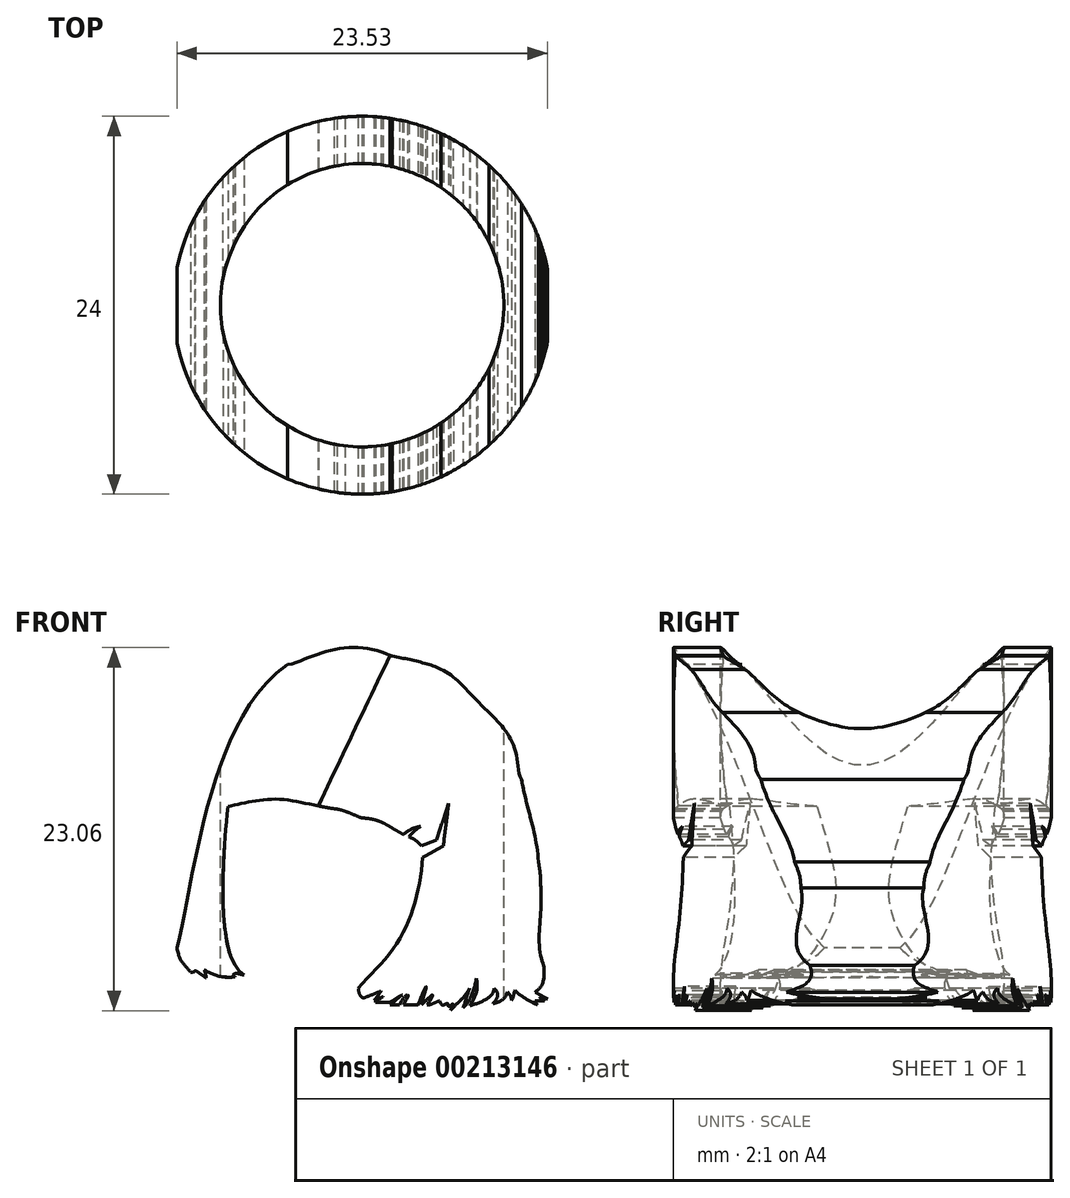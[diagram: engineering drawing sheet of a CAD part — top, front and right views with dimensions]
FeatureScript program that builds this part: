
annotation { "Feature Type Name" : "Feature", "Feature Type Description" : "" }
export const myFeature = defineFeature(function(context is Context, id is Id, definition is map)
    precondition{}
    {
        {
            var Q0;
            Q0=qCreatedBy(makeId("Top.planeOp"),FACE);
            var sketch = newSketch(context, id + "F0", { "sketchPlane" : qUnion([Q0])});
            skCircle(sketch, "E0", {"center": v(0, 0) * mm, "radius": 9 * mm});
            skCircle(sketch, "E1.0", {"center": v(0, 0) * mm, "radius": 12 * mm});
            skSolve(sketch);
        }
        {
            var Q0;
            Q0 = qSketchRegion(id + "F0", true);
            extrude(context, id + "F1", {"entities" : qUnion([Q0]), "oppositeDirection" : true, "depth" : 27.6 * mm});
        }
        {
            var Q0;
            Q0=qCreatedBy(makeId("Front.planeOp"),FACE);
            var sketch = newSketch(context, id + "F2", { "sketchPlane" : qUnion([Q0])});
            skFitSpline(sketch, "E2", {"points": [v(1.9, -2.14) * mm, v(5, -2.98) * mm], "startDerivative": vector(3.67, -0.67) * mm, "endDerivative": vector(1.76, -1) * mm});
            skFitSpline(sketch, "E3", {"points": [v(8.06, -5.72) * mm, v(5, -2.98) * mm], "startDerivative": vector(-3.05, 2.74) * mm, "endDerivative": vector(-3.1, 1.24) * mm});
            skFitSpline(sketch, "E4", {"points": [v(10.12, -9.96) * mm, v(8.06, -5.72) * mm], "startDerivative": vector(-1.55, 2.48) * mm, "endDerivative": vector(-7.13, 6.67) * mm});
            skFitSpline(sketch, "E5", {"points": [v(11.2, -16.16) * mm, v(10.12, -9.96) * mm], "startDerivative": vector(0.31, 6.82) * mm, "endDerivative": vector(-1.19, 6.77) * mm});
            skFitSpline(sketch, "E6", {"points": [v(11.53, -21.8) * mm, v(11.2, -16.16) * mm], "startDerivative": vector(-2.17, 4.8) * mm, "endDerivative": vector(-1.55, 4.96) * mm});
            skFitSpline(sketch, "E7", {"points": [v(11, -23.48) * mm, v(11.53, -21.8) * mm], "startDerivative": vector(1.31, 1.1) * mm, "endDerivative": vector(-0.27, 3.39) * mm});
            skLineSegment(sketch, "E8", {"start": v(11, -23.48) * mm, "end": v(11.77, -23.9) * mm});
            skLineSegment(sketch, "E9", {"start": v(11.77, -23.9) * mm, "end": v(11.27, -23.81) * mm});
            skLineSegment(sketch, "E10", {"start": v(11.27, -23.81) * mm, "end": v(11.58, -24.05) * mm});
            skLineSegment(sketch, "E11", {"start": v(11.58, -24.05) * mm, "end": v(10.97, -24.05) * mm});
            skLineSegment(sketch, "E12", {"start": v(10.97, -24.05) * mm, "end": v(11.13, -24.29) * mm});
            skFitSpline(sketch, "E13", {"points": [v(9.7, -23.36) * mm, v(11.13, -24.29) * mm], "startDerivative": vector(0.83, -1.03) * mm, "endDerivative": vector(1.37, -0.62) * mm});
            skFitSpline(sketch, "E14", {"points": [v(9.49, -24.02) * mm, v(9.7, -23.36) * mm], "startDerivative": vector(0.42, 0.54) * mm, "endDerivative": vector(0.2, 0.6) * mm});
            skFitSpline(sketch, "E15", {"points": [v(9.23, -23.48) * mm, v(9.49, -24.02) * mm], "startDerivative": vector(0.59, -0.48) * mm, "endDerivative": vector(0, -0.4) * mm});
            skFitSpline(sketch, "E16", {"points": [v(8.32, -24.21) * mm, v(9.23, -23.48) * mm], "startDerivative": vector(1.41, 0.44) * mm, "endDerivative": vector(0.57, 1.57) * mm});
            skFitSpline(sketch, "E17", {"points": [v(8.37, -23.25) * mm, v(8.32, -24.21) * mm], "startDerivative": vector(1.3, -0.83) * mm, "endDerivative": vector(-0.75, -0.84) * mm});
            skFitSpline(sketch, "E18", {"points": [v(6.86, -24.35) * mm, v(8.37, -23.25) * mm], "startDerivative": vector(0.44, 0.18) * mm, "endDerivative": vector(-0.17, 2.07) * mm});
            skFitSpline(sketch, "E19", {"points": [v(7.26, -22.62) * mm, v(6.86, -24.35) * mm], "startDerivative": vector(0.62, -2.35) * mm, "endDerivative": vector(-0.73, -1.3) * mm});
            skFitSpline(sketch, "E20", {"points": [v(6.41, -24.48) * mm, v(7.26, -22.62) * mm], "startDerivative": vector(1.46, 1.2) * mm, "endDerivative": vector(0.21, 1.51) * mm});
            skFitSpline(sketch, "E21", {"points": [v(6.93, -23.02) * mm, v(6.41, -24.48) * mm], "startDerivative": vector(-0.72, -1.45) * mm, "endDerivative": vector(-0.52, -1.47) * mm});
            skFitSpline(sketch, "E22", {"points": [v(5.61, -24.66) * mm, v(6.93, -23.02) * mm], "startDerivative": vector(1.32, 1.64) * mm, "endDerivative": vector(1, 2.46) * mm});
            skFitSpline(sketch, "E23", {"points": [v(5.61, -24.66) * mm, v(5.78, -24.23) * mm, v(5.5, -24.4) * mm, v(5.44, -24.2) * mm, v(5.07, -24.31) * mm, v(4.9, -24.04) * mm], "startDerivative": vector(1.45, 2.82) * mm, "endDerivative": vector(-1.44, 0.72) * mm});
            skFitSpline(sketch, "E24", {"points": [v(4.9, -24.04) * mm, v(4.13, -24.3) * mm], "startDerivative": vector(-0.77, -0.26) * mm, "endDerivative": vector(-0.9, -0.03) * mm});
            skFitSpline(sketch, "E25", {"points": [v(4.13, -24.3) * mm, v(4.5, -23.66) * mm, v(3.76, -24.3) * mm], "startDerivative": vector(1.27, 1.99) * mm, "endDerivative": vector(-1.95, -1.9) * mm});
            skFitSpline(sketch, "E26", {"points": [v(3.76, -24.3) * mm, v(4.07, -23.12) * mm, v(3.55, -24.3) * mm], "startDerivative": vector(1.03, 3.58) * mm, "endDerivative": vector(-1.44, -3.55) * mm});
            skFitSpline(sketch, "E27", {"points": [v(3.55, -24.3) * mm, v(2.64, -24.29) * mm], "startDerivative": vector(-0.9, 0.02) * mm, "endDerivative": vector(-0.9, 0.02) * mm});
            skFitSpline(sketch, "E28", {"points": [v(2.64, -24.29) * mm, v(2.91, -23.66) * mm, v(2.37, -24.29) * mm], "startDerivative": vector(0.94, 1.9) * mm, "endDerivative": vector(-0.8, -2.16) * mm});
            skLineSegment(sketch, "E29", {"start": v(2.37, -24.29) * mm, "end": v(1.79, -24.29) * mm});
            skLineSegment(sketch, "E30", {"start": v(1.79, -24.29) * mm, "end": v(2.55, -23.64) * mm});
            skLineSegment(sketch, "E31", {"start": v(2.55, -23.64) * mm, "end": v(1.79, -24.12) * mm});
            skLineSegment(sketch, "E32", {"start": v(1.79, -24.12) * mm, "end": v(0.84, -24.12) * mm});
            skLineSegment(sketch, "E33", {"start": v(0.84, -24.12) * mm, "end": v(1.34, -23.76) * mm});
            skLineSegment(sketch, "E34", {"start": v(1.34, -23.76) * mm, "end": v(0.77, -24) * mm});
            skLineSegment(sketch, "E35", {"start": v(0.77, -24) * mm, "end": v(1.22, -23.4) * mm});
            skLineSegment(sketch, "E36", {"start": v(1.22, -23.4) * mm, "end": v(0.1, -23.86) * mm});
            skFitSpline(sketch, "E37", {"points": [v(-0.37, -23.4) * mm, v(3.85, -14.92) * mm], "startDerivative": vector(4.4, 5.44) * mm, "endDerivative": vector(1.48, 16.56) * mm});
            skLineSegment(sketch, "E38", {"start": v(3.85, -14.92) * mm, "end": v(5.16, -14.18) * mm});
            skLineSegment(sketch, "E39", {"start": v(5.16, -14.18) * mm, "end": v(5.5, -11.5) * mm});
            skLineSegment(sketch, "E40", {"start": v(5.5, -11.5) * mm, "end": v(4.71, -13.82) * mm});
            skLineSegment(sketch, "E41", {"start": v(4.71, -13.82) * mm, "end": v(3.77, -14.18) * mm});
            skFitSpline(sketch, "E42", {"points": [v(3.77, -14.18) * mm, v(2.98, -13.64) * mm], "startDerivative": vector(-0.62, 0.64) * mm, "endDerivative": vector(-1.48, 0.56) * mm});
            skFitSpline(sketch, "E43", {"points": [v(2.98, -13.64) * mm, v(3.7, -12.96) * mm], "startDerivative": vector(0.3, 0.5) * mm, "endDerivative": vector(1.21, 0.88) * mm});
            skFitSpline(sketch, "E44", {"points": [v(3.7, -12.96) * mm, v(2.63, -13.46) * mm], "startDerivative": vector(-1.03, -0.16) * mm, "endDerivative": vector(-0.9, -0.83) * mm});
            skFitSpline(sketch, "E45", {"points": [v(2.63, -13.46) * mm, v(0, -12.42) * mm], "startDerivative": vector(-2.56, 1.2) * mm, "endDerivative": vector(-3.92, 0.13) * mm});
            skFitSpline(sketch, "E46", {"points": [v(2.56, -11.66) * mm, v(2, -13.11) * mm], "startDerivative": vector(-0.8, -1.46) * mm, "endDerivative": vector(-0.56, -1.45) * mm});
            skFitSpline(sketch, "E47", {"points": [v(2.56, -11.66) * mm, v(1.64, -12.9) * mm], "startDerivative": vector(-1.33, -1.28) * mm, "endDerivative": vector(-0.92, -1.25) * mm});
            skLineSegment(sketch, "E48", {"start": v(0.92, -12.57) * mm, "end": v(1.63, -11.23) * mm});
            skLineSegment(sketch, "E49", {"start": v(0.2, -12.43) * mm, "end": v(0.58, -11.95) * mm});
            skLineSegment(sketch, "E50", {"start": v(0.58, -11.95) * mm, "end": v(0.58, -12.49) * mm});
            skFitSpline(sketch, "E51", {"points": [v(0, -12.42) * mm, v(-1.78, -11.84) * mm], "startDerivative": vector(-1.7, 0.57) * mm, "endDerivative": vector(-1.71, 0.07) * mm});
            skLineSegment(sketch, "E52", {"start": v(-1.57, -11.86) * mm, "end": v(-0.12, -9.62) * mm});
            skLineSegment(sketch, "E53", {"start": v(-0.12, -9.62) * mm, "end": v(-1.1, -11.99) * mm});
            skFitSpline(sketch, "E54", {"points": [v(-8.53, -11.68) * mm, v(-1.78, -11.84) * mm], "startDerivative": vector(11.15, 2.5) * mm, "endDerivative": vector(9.81, -1.6) * mm});
            skFitSpline(sketch, "E55", {"points": [v(-8.53, -11.68) * mm, v(-7.5, -22.38) * mm], "startDerivative": vector(-0.8, -8.26) * mm, "endDerivative": vector(5.78, -3.37) * mm});
            skFitSpline(sketch, "E56", {"points": [v(-7.5, -22.38) * mm, v(-8.18, -22.38) * mm], "startDerivative": vector(-0.68, 0) * mm, "endDerivative": vector(-0.4, -0.62) * mm});
            skFitSpline(sketch, "E57", {"points": [v(-8.18, -22.38) * mm, v(-8.06, -22.51) * mm], "startDerivative": vector(0.05, -0.18) * mm, "endDerivative": vector(0.16, -0.12) * mm});
            skFitSpline(sketch, "E58", {"points": [v(-8.06, -22.51) * mm, v(-10.02, -22.07) * mm], "startDerivative": vector(-1.9, -0.21) * mm, "endDerivative": vector(-2.14, 1.36) * mm});
            skFitSpline(sketch, "E59", {"points": [v(-0.24, -23.24) * mm, v(0.1, -23.86) * mm], "startDerivative": vector(0.23, -1.34) * mm, "endDerivative": vector(0.68, -0.3) * mm});
            skFitSpline(sketch, "E60", {"points": [v(-10.02, -22.07) * mm, v(-9.91, -22.6) * mm], "startDerivative": vector(0.25, -0.86) * mm, "endDerivative": vector(-0.08, -0.15) * mm});
            skFitSpline(sketch, "E61", {"points": [v(-10.6, -22.1) * mm, v(-9.91, -22.6) * mm], "startDerivative": vector(0.69, -0.5) * mm, "endDerivative": vector(0.86, -0.75) * mm});
            skFitSpline(sketch, "E62", {"points": [v(-10.6, -22.1) * mm, v(-10.66, -22.3) * mm], "startDerivative": vector(-0.22, -0.22) * mm, "endDerivative": vector(0, -0.14) * mm});
            skFitSpline(sketch, "E63", {"points": [v(-10.65, -22.2) * mm, v(-10.89, -22.21) * mm], "startDerivative": vector(-0.24, 0) * mm, "endDerivative": vector(-0.24, 0) * mm});
            skFitSpline(sketch, "E64", {"points": [v(-10.89, -22.21) * mm, v(-11.76, -20.67) * mm], "startDerivative": vector(-1.15, 1.53) * mm, "endDerivative": vector(-0.5, 2.86) * mm});
            skFitSpline(sketch, "E65", {"points": [v(-11.76, -20.67) * mm, v(-4.73, -2.68) * mm], "startDerivative": vector(3.52, 14.57) * mm, "endDerivative": vector(14.71, 9.94) * mm});
            skFitSpline(sketch, "E66", {"points": [v(-4.73, -2.68) * mm, v(1.9, -2.14) * mm], "startDerivative": vector(2.86, 0.15) * mm, "endDerivative": vector(9.8, -4.4) * mm});
            skFitSpline(sketch, "E67", {"points": [v(11.2, -15.21) * mm, v(11.35, -16.86) * mm], "startDerivative": vector(0.23, -1.37) * mm, "endDerivative": vector(0, -2.47) * mm});
            skFitSpline(sketch, "E68", {"points": [v(1.63, -11.23) * mm, v(1.28, -12.71) * mm], "startDerivative": vector(-0.35, -1.48) * mm, "endDerivative": vector(0.12, -1.22) * mm});
            skLineSegment(sketch, "E69.bottom", {"start": v(-14.42, 1.64) * mm, "end": v(13.8, 1.64) * mm});
            skLineSegment(sketch, "E69.top", {"start": v(-14.42, -28.62) * mm, "end": v(13.8, -28.62) * mm});
            skLineSegment(sketch, "E69.left", {"start": v(-14.42, 1.64) * mm, "end": v(-14.42, -28.62) * mm});
            skLineSegment(sketch, "E69.right", {"start": v(13.8, 1.64) * mm, "end": v(13.8, -28.62) * mm});
            skSolve(sketch);
        }
        {
            var Q0;
            Q0 = qSketchRegion(id + "F2", true);
            extrude(context, id + "F3", {"entities" : qUnion([Q0]), "operationType" : NewBodyOperationType.REMOVE, "endBound" : BoundingType.SYMMETRIC, "oppositeDirection" : true, "depth" : 32.8 * mm});
        }
        {
            var Q0;
            Q0=qCreatedBy(makeId("Front.planeOp"),FACE);
            var sketch = newSketch(context, id + "F4", { "sketchPlane" : qUnion([Q0])});
            skLineSegment(sketch, "E70", {"start": v(2.68, -0.19) * mm, "end": v(-3.94, -14.08) * mm});
            skLineSegment(sketch, "E71", {"start": v(-3.94, -14.08) * mm, "end": v(-3.94, -14.08) * mm});
            skLineSegment(sketch, "E72", {"start": v(-3.94, -14.08) * mm, "end": v(2.68, -0.19) * mm});
            skLineSegment(sketch, "E73", {"start": v(2.68, -0.19) * mm, "end": v(2.68, -0.19) * mm});
            skSolve(sketch);
        }
        {
            var Q0;
            Q0 = qSketchRegion(id + "F4", true);
            extrude(context, id + "F5", {"entities" : qUnion([Q0]), "operationType" : NewBodyOperationType.REMOVE, "endBound" : BoundingType.SYMMETRIC, "oppositeDirection" : true, "depth" : 39.2 * mm});
        }
    });
